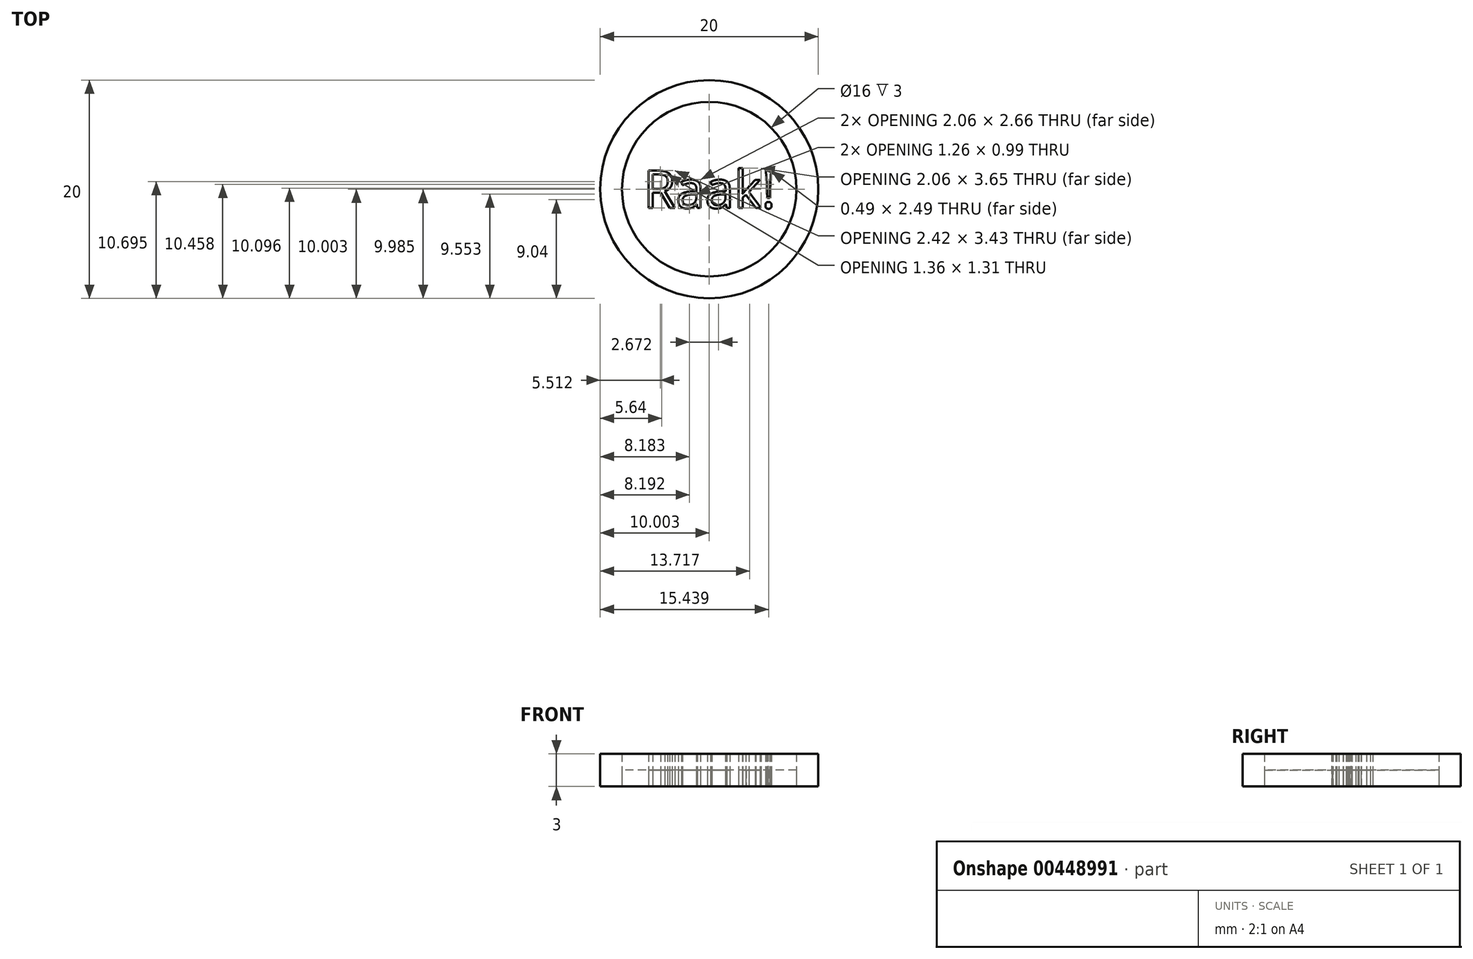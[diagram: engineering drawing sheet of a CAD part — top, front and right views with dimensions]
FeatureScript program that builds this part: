
annotation { "Feature Type Name" : "Feature", "Feature Type Description" : "" }
export const myFeature = defineFeature(function(context is Context, id is Id, definition is map)
    precondition{}
    {
        {
            var Q0;
            Q0=qCreatedBy(makeId("Top.planeOp"),FACE);
            var sketch = newSketch(context, id + "F0", { "sketchPlane" : qUnion([Q0])});
            skText(sketch, "E0", { "text": "Raak!", "fontName": "OpenSans-Regular.ttf"});
            skCircle(sketch, "E1", {"center": v(-7.64, -17.87) * mm, "radius": 10 * mm});
            skCircle(sketch, "E2", {"center": v(-7.64, -17.87) * mm, "radius": 8 * mm});
            const initialGuessF0  = {"E0": [-0.01368, -0.0196, 1, 0, 0.00346]};
            skSetInitialGuess(sketch, initialGuessF0);
            skSolve(sketch);
        }
        {
            var Q0;
            Q0 = qSketchRegion(id + "F0", true);
            var Q1;
            Q1=makeQuery(id+"F0.imprint","IMPRINT",FACE,{"disambiguationData":[TD([[makeQuery(id+"F0.imprint","IMPRINT",EDGE,{"derivedFrom":sQuery(id+"F0.wireOp",EDGE,"E0.sketch_text.stroke-0")}),-1.0]])]});
            var Q2;
            Q2=makeQuery(id+"F0.imprint","IMPRINT",FACE,{"disambiguationData":[TD([[makeQuery(id+"F0.imprint","IMPRINT",EDGE,{"derivedFrom":sQuery(id+"F0.wireOp",EDGE,"E0.sketch_text.stroke-18")}),-1.0]])]});
            var Q3;
            Q3=makeQuery(id+"F0.imprint","IMPRINT",FACE,{"disambiguationData":[TD([[makeQuery(id+"F0.imprint","IMPRINT",EDGE,{"derivedFrom":sQuery(id+"F0.wireOp",EDGE,"E0.sketch_text.stroke-45")}),-1.0]])]});
            var Q4;
            Q4=makeQuery(id+"F0.imprint","IMPRINT",FACE,{"disambiguationData":[TD([[makeQuery(id+"F0.imprint","IMPRINT",EDGE,{"derivedFrom":sQuery(id+"F0.wireOp",EDGE,"E0.sketch_text.stroke-72")}),-1.0]])]});
            var Q5;
            Q5=makeQuery(id+"F0.imprint","IMPRINT",FACE,{"disambiguationData":[TD([[makeQuery(id+"F0.imprint","IMPRINT",EDGE,{"derivedFrom":sQuery(id+"F0.wireOp",EDGE,"E0.sketch_text.stroke-91")}),-1.0]])]});
            var Q6;
            Q6=makeQuery(id+"F0.imprint","IMPRINT",FACE,{"disambiguationData":[TD([[makeQuery(id+"F0.imprint","IMPRINT",EDGE,{"derivedFrom":sQuery(id+"F0.wireOp",EDGE,"E0.sketch_text.stroke-87")}),-1.0]])]});
            extrude(context, id + "F1", {"entities" : qUnion([Q0, Q1, Q2, Q3, Q4, Q5, Q6]), "depth" : 3 * mm});
        }
        {
            var Q0;
            Q0=makeQuery(id+"F0.imprint","IMPRINT",FACE,{"disambiguationData":[TD([[makeQuery(id+"F0.imprint","IMPRINT",EDGE,{"derivedFrom":sQuery(id+"F0.wireOp",EDGE,"E0.sketch_text.stroke-0")}),1.0]])]});
            var Q1;
            Q1=makeQuery(id+"F0.imprint","IMPRINT",FACE,{"disambiguationData":[TD([[makeQuery(id+"F0.imprint","IMPRINT",EDGE,{"derivedFrom":sQuery(id+"F0.wireOp",EDGE,"E0.sketch_text.stroke-11")}),1.0]])]});
            var Q2;
            Q2=makeQuery(id+"F0.imprint","IMPRINT",FACE,{"disambiguationData":[TD([[makeQuery(id+"F0.imprint","IMPRINT",EDGE,{"derivedFrom":sQuery(id+"F0.wireOp",EDGE,"E0.sketch_text.stroke-37")}),1.0]])]});
            var Q3;
            Q3=makeQuery(id+"F0.imprint","IMPRINT",FACE,{"disambiguationData":[TD([[makeQuery(id+"F0.imprint","IMPRINT",EDGE,{"derivedFrom":sQuery(id+"F0.wireOp",EDGE,"E0.sketch_text.stroke-64")}),1.0]])]});
            extrude(context, id + "F2", {"entities" : qUnion([Q0, Q1, Q2, Q3]), "depth" : 1.5 * mm});
        }
    });
